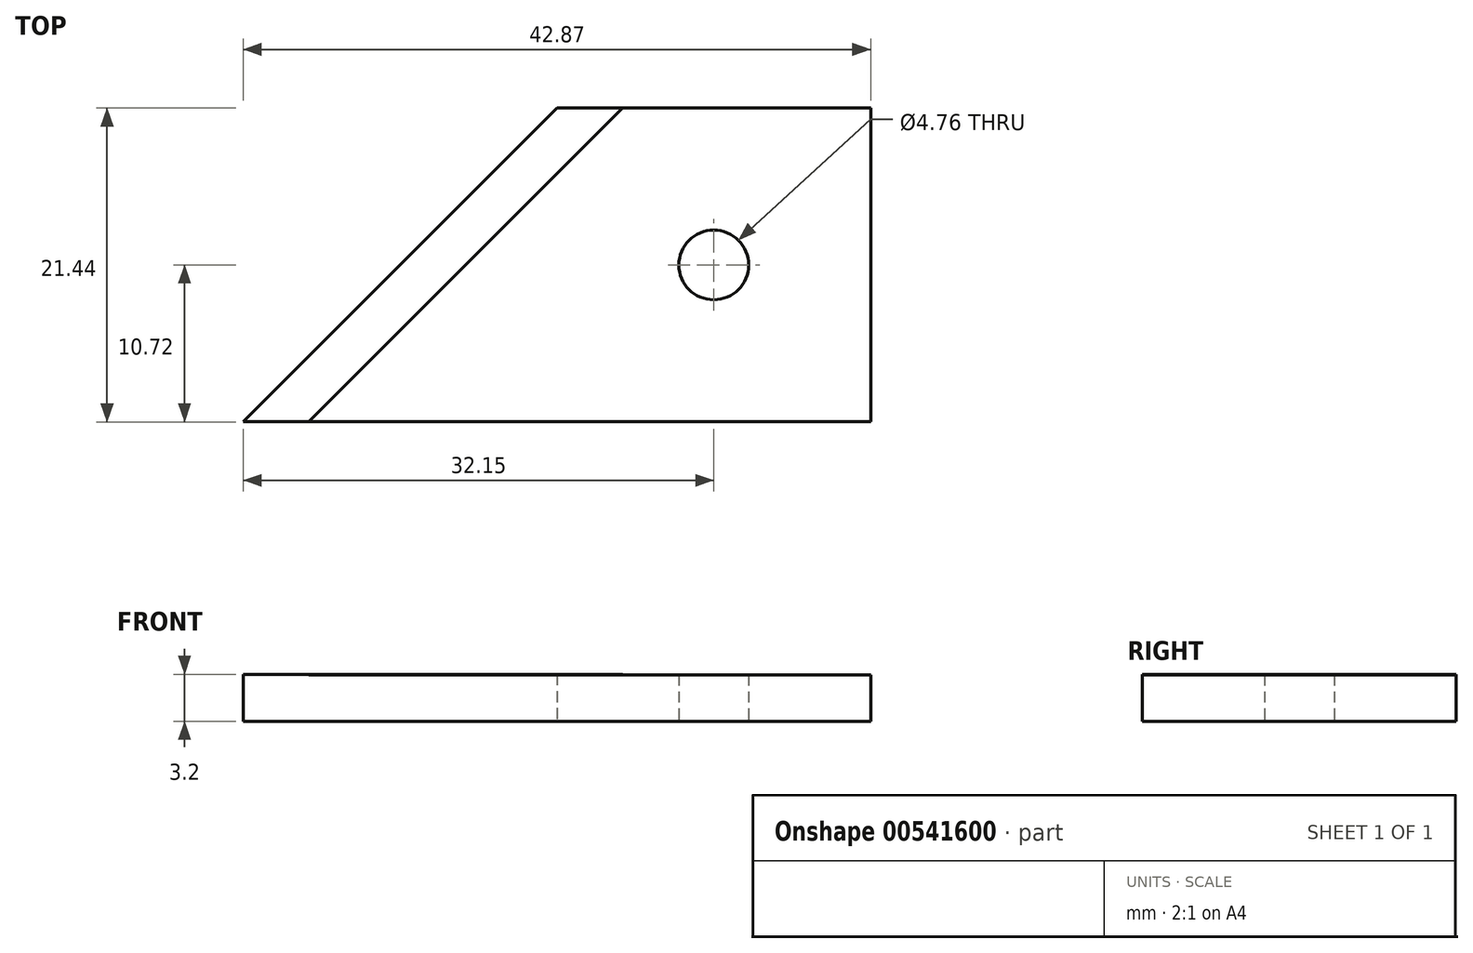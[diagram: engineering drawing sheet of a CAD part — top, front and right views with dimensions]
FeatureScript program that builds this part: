
annotation { "Feature Type Name" : "Feature", "Feature Type Description" : "" }
export const myFeature = defineFeature(function(context is Context, id is Id, definition is map)
    precondition{}
    {
        {
            var Q0;
            Q0=qCreatedBy(makeId("Top.planeOp"),FACE);
            var sketch = newSketch(context, id + "F0", { "sketchPlane" : qUnion([Q0])});
            skLineSegment(sketch, "E0.bottom", {"start": v(-10.72, 10.72) * mm, "end": v(10.72, 10.72) * mm});
            skLineSegment(sketch, "E0.top", {"start": v(-10.72, -10.72) * mm, "end": v(10.72, -10.72) * mm});
            skLineSegment(sketch, "E0.left", {"start": v(-10.72, 10.72) * mm, "end": v(-10.72, -10.72) * mm});
            skLineSegment(sketch, "E0.right", {"start": v(10.72, 10.72) * mm, "end": v(10.72, -10.72) * mm});
            skPoint(sketch, "E0.middle", {"position": v(0, 0) * mm});
            skCircle(sketch, "E1", {"center": v(0, 0) * mm, "radius": 2.38 * mm});
            skLineSegment(sketch, "E2.MirrorCS", {"start": v(-32.15, -10.72) * mm, "end": v(-10.72, 10.72) * mm});
            skLineSegment(sketch, "E3.MirrorCS", {"start": v(-10.72, -10.72) * mm, "end": v(-32.15, -10.72) * mm});
            skSolve(sketch);
        }
        {
            var Q0;
            Q0=qSketchRegion(id+"F0",true);
            extrude(context, id + "F1", {"entities" : qUnion([Q0]), "depth" : 3.17 * mm, "offsetDistance" : 25.4 * mm});
        }
        {
            var Q0;
            Q0=makeQuery(id+"F1.opExtrude","CAP_FACE",FACE,{"disambiguationData":[OSD([sQuery(id+"F0.wireOp",EDGE,"E0.bottom"),sQuery(id+"F0.wireOp",EDGE,"E0.top"),sQuery(id+"F0.wireOp",EDGE,"E0.left"),sQuery(id+"F0.wireOp",EDGE,"wlNkNfzO-yuzW-12TG-TpRq-uvKJH9jwdXxn"),sQuery(id+"F0.wireOp",EDGE,"s9pMNwbS-aARZ-WTIJ-v88e-64NB7hbVvaPj")])],"isStart":false});
            var sketch = newSketch(context, id + "F2", { "sketchPlane" : qUnion([Q0])});
            skLineSegment(sketch, "E4.MirrorCS", {"start": v(-8.47, 8.47) * mm, "end": v(-27.66, -10.72) * mm});
            skLineSegment(sketch, "E5.MirrorCS", {"start": v(-10.72, 10.72) * mm, "end": v(-32.15, -10.72) * mm});
            skLineSegment(sketch, "E6.MirrorCS", {"start": v(-32.15, -10.72) * mm, "end": v(-27.66, -10.72) * mm});
            skLineSegment(sketch, "E7.MirrorCS", {"start": v(-6.23, 10.72) * mm, "end": v(-10.72, 10.72) * mm});
            skLineSegment(sketch, "E8.MirrorCS", {"start": v(-8.47, 8.47) * mm, "end": v(-6.23, 10.72) * mm});
            skSolve(sketch);
        }
        {
            var Q0;
            Q0=qSketchRegion(id+"F2",true);
            extrude(context, id + "F3", {"entities" : qUnion([Q0]), "operationType" : NewBodyOperationType.ADD, "depth" : 11.5 / 406.4 * mm, "offsetDistance" : 25.4 * mm});
        }
    });
